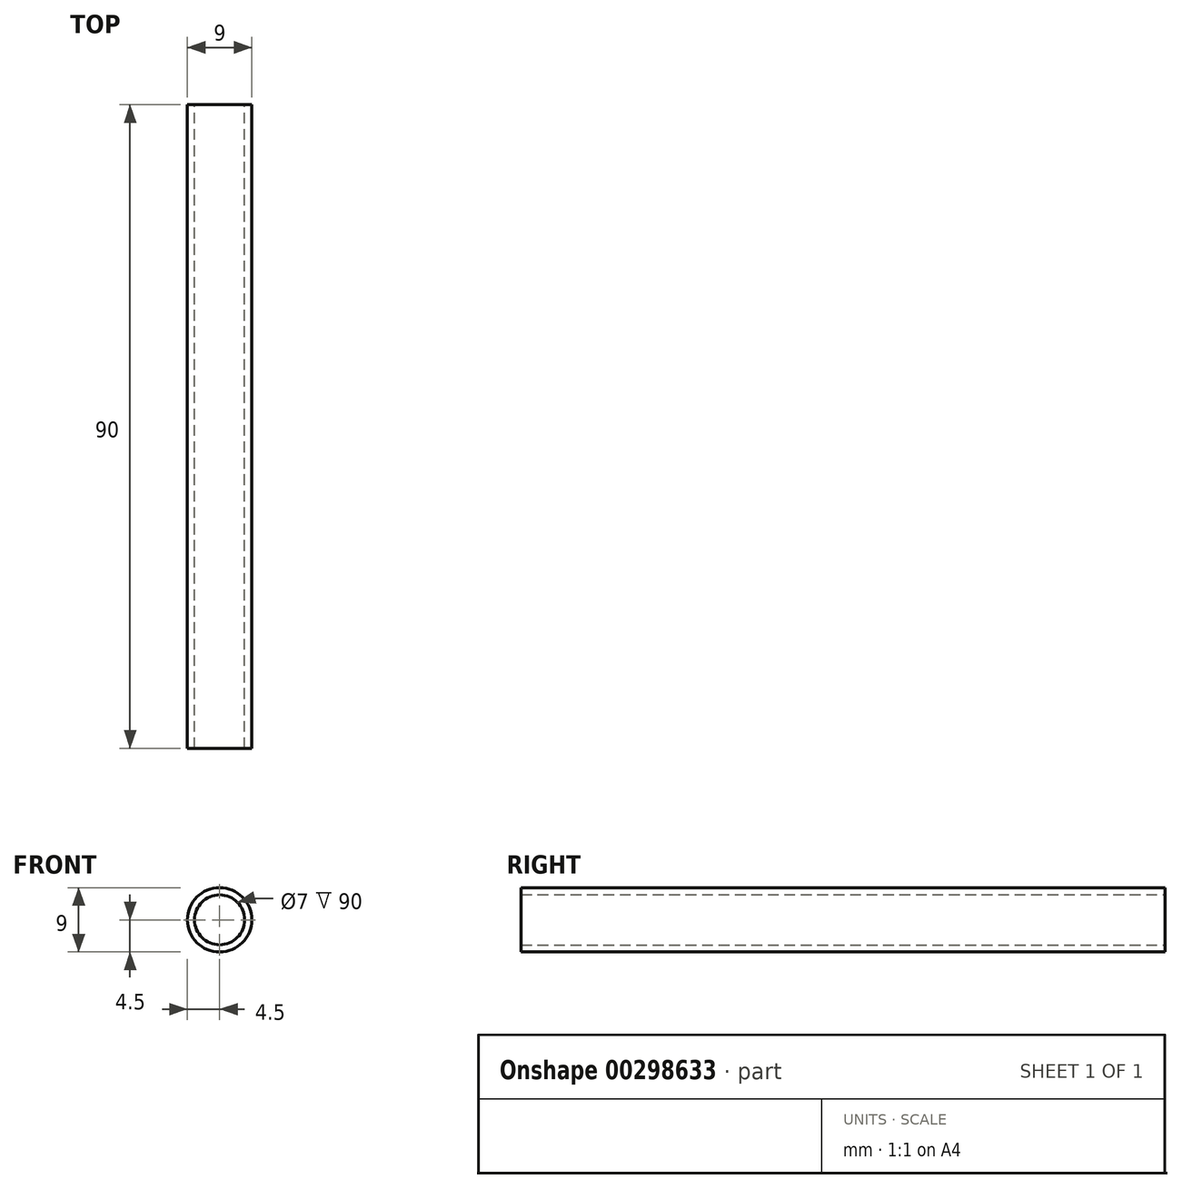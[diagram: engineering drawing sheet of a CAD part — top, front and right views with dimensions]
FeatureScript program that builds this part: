
annotation { "Feature Type Name" : "Feature", "Feature Type Description" : "" }
export const myFeature = defineFeature(function(context is Context, id is Id, definition is map)
    precondition{}
    {
        {
            var Q0;
            Q0=qCreatedBy(makeId("Front.planeOp"),FACE);
            var sketch = newSketch(context, id + "F0", { "sketchPlane" : qUnion([Q0])});
            skCircle(sketch, "E0", {"center": v(0, 0) * mm, "radius": 4.5 * mm});
            skCircle(sketch, "E1", {"center": v(0, 0) * mm, "radius": 3.5 * mm});
            skSolve(sketch);
        }
        {
            var Q0;
            Q0=makeQuery(id+"F0.imprint","IMPRINT",FACE,{"disambiguationData":[TD([[makeQuery(id+"F0.imprint","IMPRINT",EDGE,{"derivedFrom":sQuery(id+"F0.wireOp",EDGE,"E0")}),1.0]])]});
            extrude(context, id + "F1", {"entities" : qUnion([Q0]), "depth" : 90 * mm});
        }
    });
